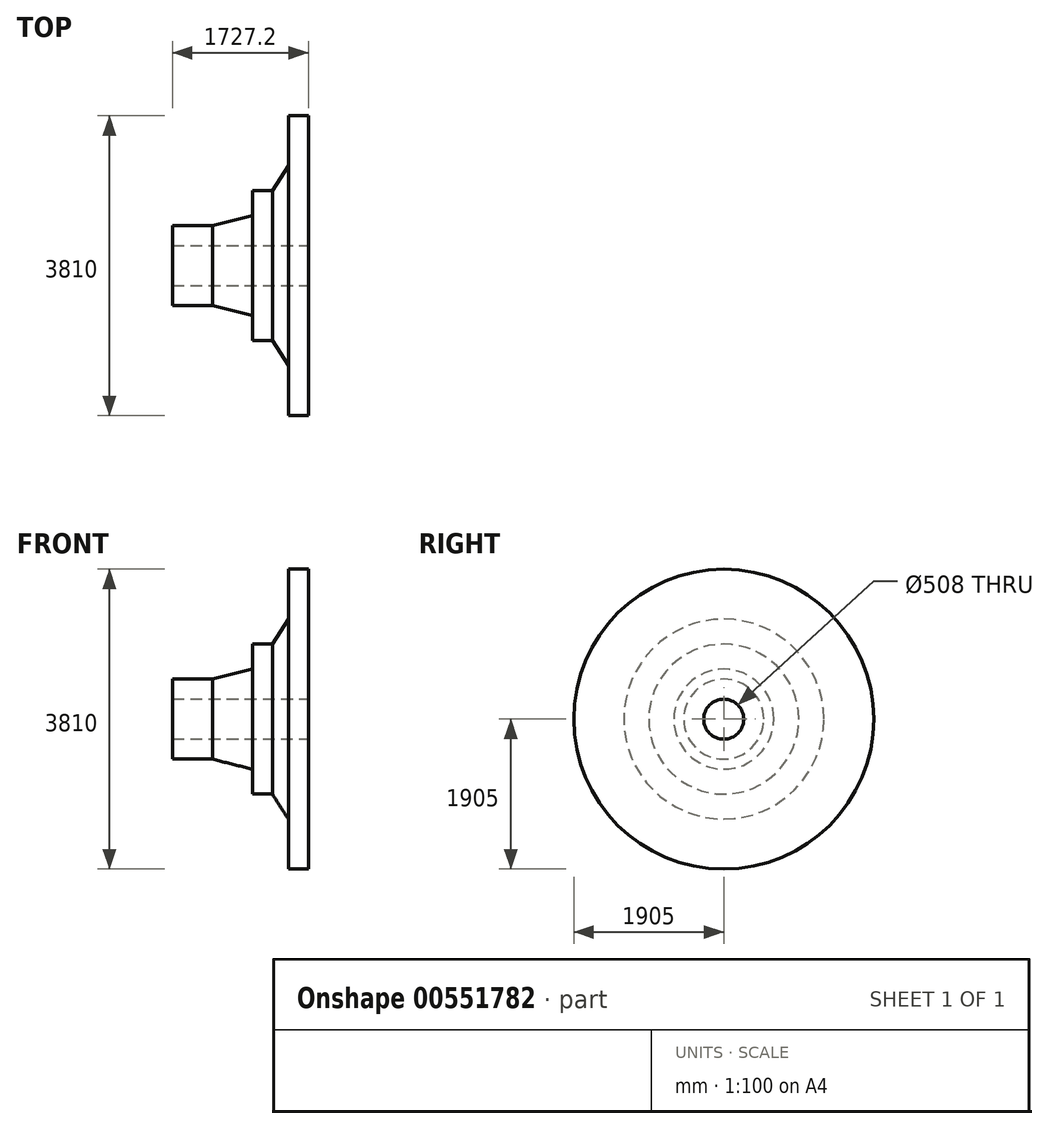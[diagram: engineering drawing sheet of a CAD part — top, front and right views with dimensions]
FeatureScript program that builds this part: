
annotation { "Feature Type Name" : "Feature", "Feature Type Description" : "" }
export const myFeature = defineFeature(function(context is Context, id is Id, definition is map)
    precondition{}
    {
        {
            var Q0;
            Q0=qCreatedBy(makeId("Front.planeOp"),FACE);
            var sketch = newSketch(context, id + "F0", { "sketchPlane" : qUnion([Q0])});
            skLineSegment(sketch, "E0", {"start": v(888.42, -666.62) * mm, "end": v(-838.78, -666.62) * mm});
            skLineSegment(sketch, "E1", {"start": v(-838.78, -666.62) * mm, "end": v(-838.78, -412.62) * mm});
            skLineSegment(sketch, "E2", {"start": v(-838.78, -412.62) * mm, "end": v(-330.78, -412.62) * mm});
            skLineSegment(sketch, "E3", {"start": v(-330.78, -412.62) * mm, "end": v(177.22, -285.62) * mm});
            skLineSegment(sketch, "E4", {"start": v(431.22, 31.88) * mm, "end": v(634.42, 349.38) * mm});
            skLineSegment(sketch, "E5", {"start": v(634.42, 349.38) * mm, "end": v(634.42, 984.38) * mm});
            skLineSegment(sketch, "E6", {"start": v(634.42, 984.38) * mm, "end": v(888.42, 984.38) * mm});
            skLineSegment(sketch, "E7", {"start": v(888.42, 984.38) * mm, "end": v(888.42, -666.62) * mm});
            skLineSegment(sketch, "E8", {"start": v(177.22, -285.62) * mm, "end": v(177.22, 31.88) * mm});
            skLineSegment(sketch, "E9", {"start": v(177.22, 31.88) * mm, "end": v(431.22, 31.88) * mm});
            skLineSegment(sketch, "E10", {"start": v(959.7, -920.62) * mm, "end": v(-1665.43, -920.62) * mm});
            skSolve(sketch);
        }
        {
            var Q0;
            Q0=qSketchRegion(id+"F0",true);
            var Q1;
            Q1=sQuery(id+"F0.wireOp",EDGE,"E10");
            revolve(context, id + "F1", {"entities" : qUnion([Q0]), "axis" : qUnion([Q1]), "revolveType" : RevolveType.FULL});
        }
    });
